# Revit family: FU_Table_Sandler_Stiks 8-2
name_source: partatom
category: Furniture
units: mm (PartAtom-declared; Revit-internal decimal feet)

## family parameters
Always vertical = Yes
Cut with Voids When Loaded = No
OmniClass Number = 23.40.20.00
OmniClass Title = General Furniture and Specialties
Room Calculation Point = No
Shared = No
Work Plane-Based = No

## types (3) — shared parameters
Description = Table with top and legs in natural oak. Tops and legs are available in natural oak color, lacquered or varnished.
Frame Depth = 505 mm  [stored 1.65682 ft]
Frame Width = 505 mm  [stored 1.65682 ft]
Height = 750 mm  [stored 2.46063 ft]
Manufacturer = Sandler
Model = Stiks 8.2
URL = https://www.sandlerseating.com
zero-valued in all types: Default Elevation

## per-type parameters (varying)
| type | Top Size |
| Stiks 8.2 - 60cm / 24" Top | IC_TAP_Round : TAP0060 - 60cm / 24" Diameter |
| Stiks 8.2 - 70cm / 28" Top | IC_TAP_Round : TAP0070 - 70cm / 28" Diameter |
| Stiks 8.2 - 80cm / 32" Top | IC_TAP_Round : TAP0080 - 80cm / 32" Diameter |

note: [stored X ft] marks values corroborated as IEEE doubles in the binary element streams (Revit-internal decimal feet)

## geometry (parser evidence)
native form markers: Sweep x6
no freeform markers — native parametric forms only
